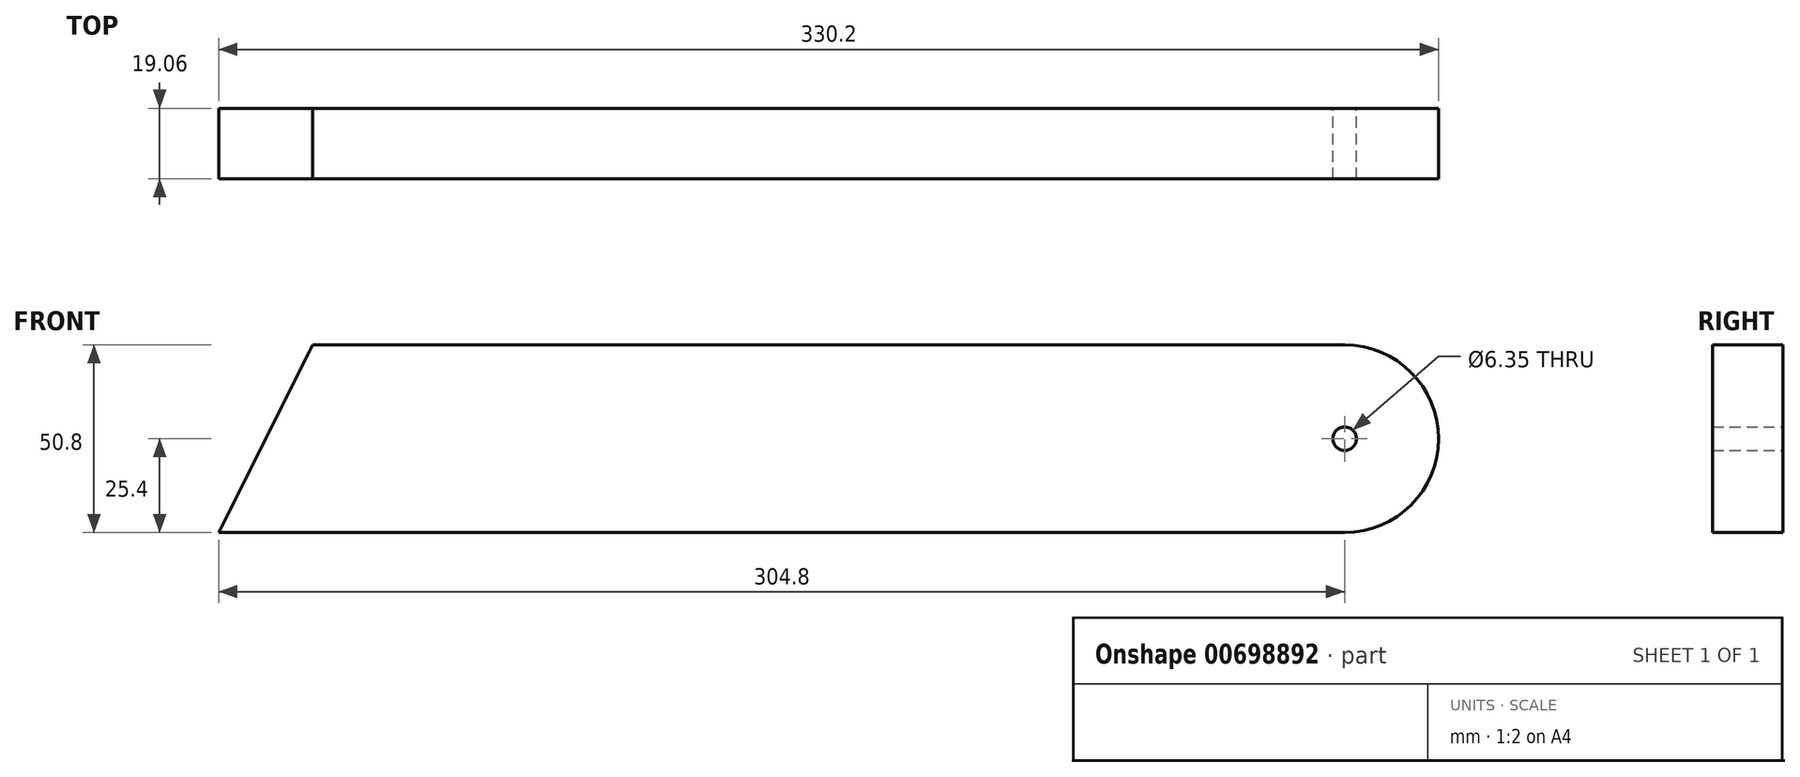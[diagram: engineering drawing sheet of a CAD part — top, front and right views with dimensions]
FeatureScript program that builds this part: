
annotation { "Feature Type Name" : "Feature", "Feature Type Description" : "" }
export const myFeature = defineFeature(function(context is Context, id is Id, definition is map)
    precondition{}
    {
        {
            var Q0;
            Q0=qCreatedBy(makeId("Front.planeOp"),FACE);
            var sketch = newSketch(context, id + "F0", { "sketchPlane" : qUnion([Q0])});
            skPoint(sketch, "E0.middle", {"position": v(0, 0) * mm});
            skCircle(sketch, "E1", {"center": v(139.7, 0) * mm, "radius": 25.4 * mm});
            skCircle(sketch, "E2", {"center": v(139.7, 0) * mm, "radius": 3.18 * mm});
            skLineSegment(sketch, "E3.bottom", {"start": v(139.7, 25.4) * mm, "end": v(-139.7, 25.4) * mm});
            skLineSegment(sketch, "E3.top", {"start": v(139.7, -25.4) * mm, "end": v(-139.7, -25.4) * mm});
            skLineSegment(sketch, "E3.left", {"start": v(139.7, 25.4) * mm, "end": v(139.7, -25.4) * mm});
            skLineSegment(sketch, "E3.right", {"start": v(-139.7, 25.4) * mm, "end": v(-139.7, -25.4) * mm});
            skLineSegment(sketch, "E4", {"start": v(-139.7, -25.4) * mm, "end": v(-165.1, -25.4) * mm});
            skLineSegment(sketch, "E5", {"start": v(-165.1, -25.4) * mm, "end": v(-139.7, 25.4) * mm});
            skSolve(sketch);
        }
        {
            var Q0;
            Q0 = qSketchRegion(id + "F0", true);
            extrude(context, id + "F1", {"entities" : qUnion([Q0]), "endBound" : BoundingType.SYMMETRIC, "depth" : 19.05 * mm, "offsetDistance" : 25.4 * mm});
        }
    });
